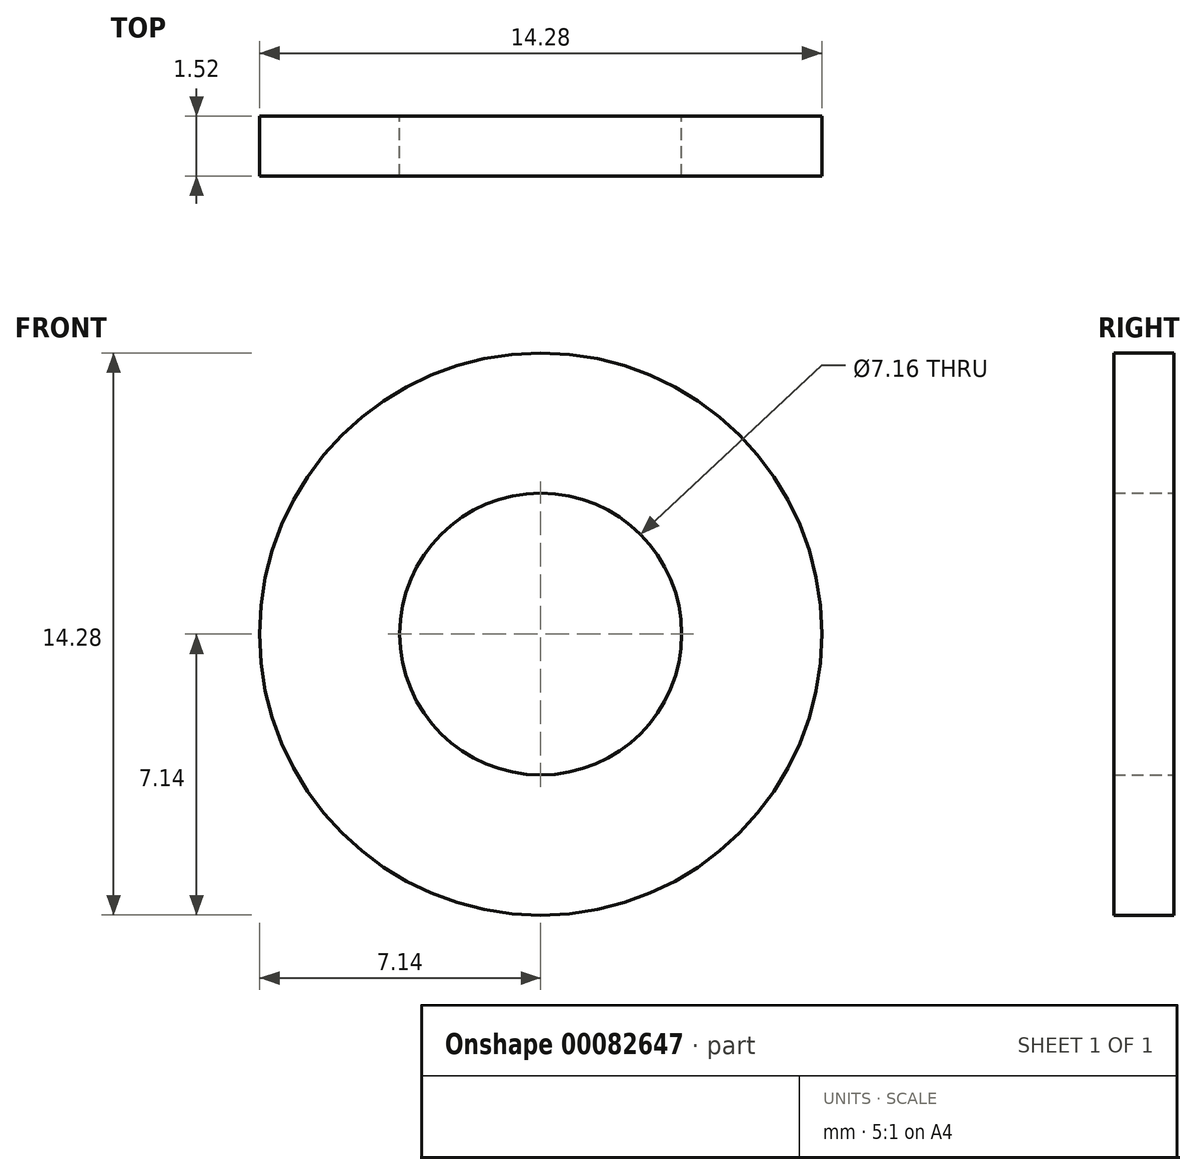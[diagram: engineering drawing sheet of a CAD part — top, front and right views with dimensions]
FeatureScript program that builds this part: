
annotation { "Feature Type Name" : "Feature", "Feature Type Description" : "" }
export const myFeature = defineFeature(function(context is Context, id is Id, definition is map)
    precondition{}
    {
        {
            var Q0;
            Q0=qCreatedBy(makeId("Front.planeOp"),FACE);
            var sketch = newSketch(context, id + "F0", { "sketchPlane" : qUnion([Q0])});
            skCircle(sketch, "E0", {"center": v(0, 0) * mm, "radius": 7.14 * mm});
            skCircle(sketch, "E1", {"center": v(0, 0) * mm, "radius": 3.58 * mm});
            skSolve(sketch);
        }
        {
            var Q0;
            Q0 = qSketchRegion(id + "F0", true);
            extrude(context, id + "F1", {"entities" : qUnion([Q0]), "depth" : 1.52 * mm});
        }
    });
